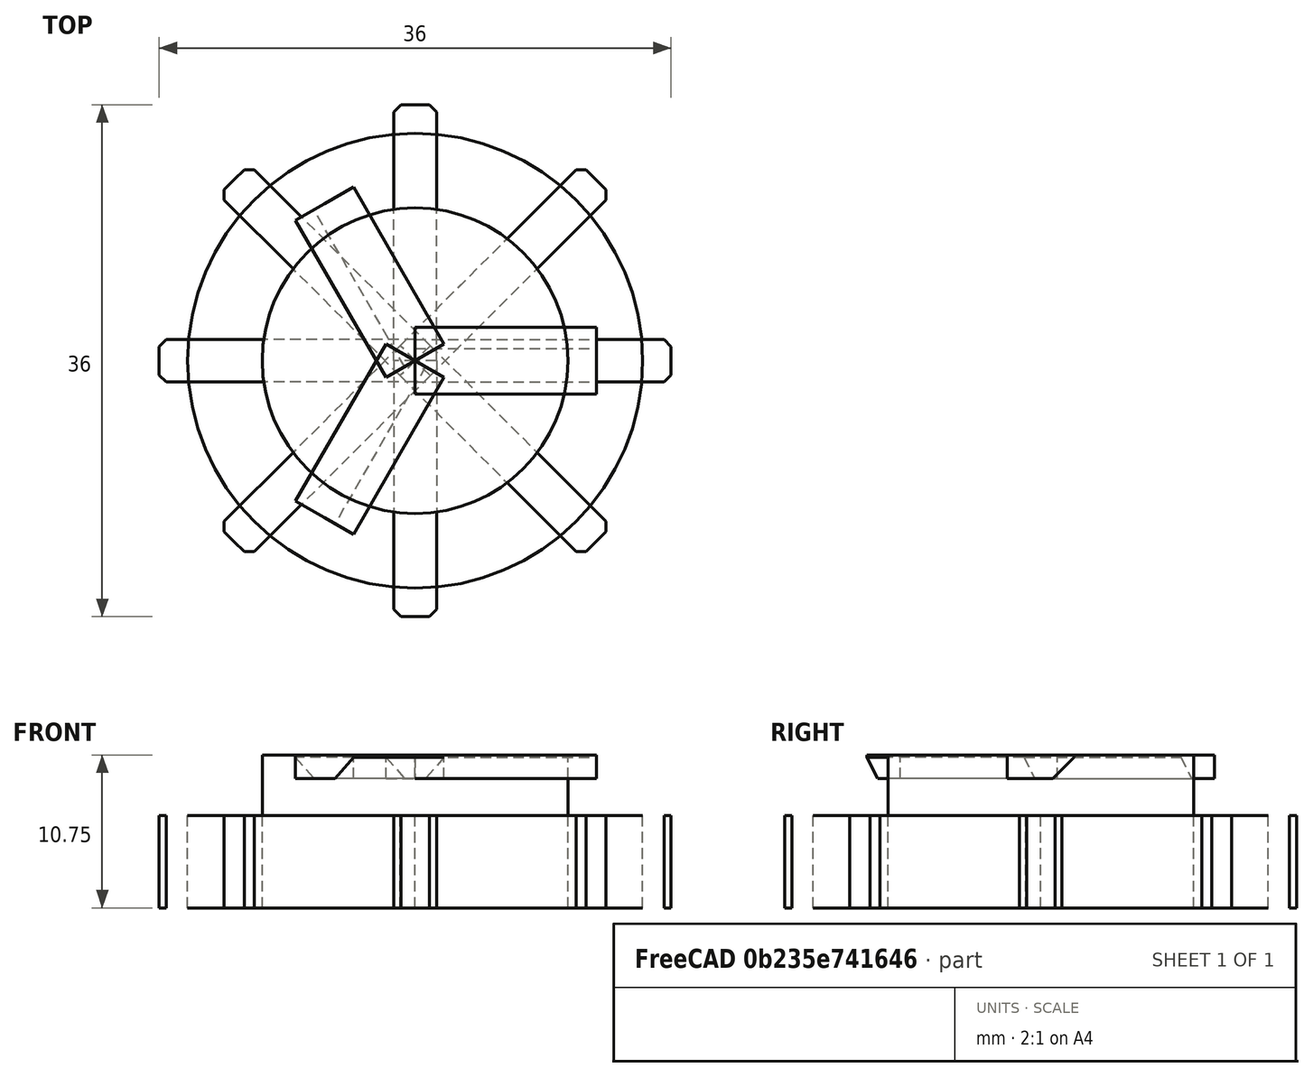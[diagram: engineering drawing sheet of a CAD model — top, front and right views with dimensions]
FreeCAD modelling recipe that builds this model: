
FCSTD DOCUMENT  (FreeCAD 0.18R16146 (Git))
Label: maleBayonetFCV1
License: All rights reserved
LicenseURL: http://en.wikipedia.org/wiki/All_rights_reserved
objects: Part::Box×4, Part::Chamfer×3, Part::Cylinder×2, Part::MultiFuse×2, Part::FeaturePython×2
note: 13 computed .brp shape members not serialized (recipe doc carries the construction recipe); baked Part::Feature solids carry a one-line shape summary decoded from their .brp

FEATURE [Part::Cylinder] Cylinder001
  Angle = 360
  AttacherType = Attacher::AttachEngine3D
  Height = 6.5
  Radius = 16
FEATURE [Part::Box] Box  label="Cube"
  AttacherType = Attacher::AttachEngine3D
  Height = 6.5
  Length = 18
  Width = 1.5
FEATURE [Part::Box] Box001  label="Cube001"
  AttacherType = Attacher::AttachEngine3D
  Height = 6.5
  Length = 18
  Placement = pos=(0,-1.5,0) rot=(0,0,1;0rad)
  Width = 1.5
FEATURE [Part::Chamfer] Chamfer
  Base = -> Box
  Edges = 1 edges r=0.5: [Edge7]
FEATURE [Part::Chamfer] Chamfer001
  Base = -> Box001
  Edges = 1 edges r=0.5: [Edge5]
FEATURE [Part::MultiFuse] Fusion
  Shapes = -> [Chamfer001,Chamfer]
FEATURE [Part::FeaturePython] Array  # Draft array (typed FeaturePython)
  Angle = 360
  ArrayType = 1
  Axis = (0,0,1)
  Base = -> Fusion
  Center = (0,0,0)
  Fuse = false
  IntervalAxis = (0,0,0)
  IntervalX = (1,0,0)
  IntervalY = (0,1,0)
  IntervalZ = (0,0,1)
  NumberPolar = 8
  NumberX = 2
  NumberY = 2
  NumberZ = 1
FEATURE [Part::Cylinder] Cylinder
  Angle = 360
  AttacherType = Attacher::AttachEngine3D
  Height = 10.75
  Radius = 10.75
FEATURE [Part::Box] Box002  label="Cube002"
  AttacherType = Attacher::AttachEngine3D
  Height = 1.65
  Length = 12.75
  Placement = pos=(0,0,9.1) rot=(0,0,1;0rad)
  Width = 2.35
FEATURE [Part::Box] Box003  label="Cube003"
  AttacherType = Attacher::AttachEngine3D
  Height = 1.65
  Length = 12.75
  Placement = pos=(0,-2.35,9.1) rot=(0,0,1;0rad)
  Width = 2.35
FEATURE [Part::MultiFuse] Fusion001
  Shapes = -> [Box003,Box002]
FEATURE [Part::Chamfer] Chamfer002
  Base = -> Fusion001
  Edges = 1 edges r=1.5: [Edge18]
FEATURE [Part::FeaturePython] Array001  # Draft array (typed FeaturePython)
  Angle = 360
  ArrayType = 1
  Axis = (0,0,1)
  Base = -> Chamfer002
  Center = (0,0,0)
  Fuse = false
  IntervalAxis = (0,0,0)
  IntervalX = (1,0,0)
  IntervalY = (0,1,0)
  IntervalZ = (0,0,1)
  NumberPolar = 3
  NumberX = 2
  NumberY = 2
  NumberZ = 1
